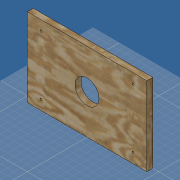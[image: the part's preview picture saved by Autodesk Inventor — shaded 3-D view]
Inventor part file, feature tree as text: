
AUTODESK INVENTOR PART (.ipt)
format: ipt  version: 2019 (Build 230136000, 136)  size: 135,168 bytes
history: native  units: mm
features: extrude x2, other x1, sketch x1
ambient origin geometry x8: Origin, YZ Plane, XZ Plane, XY Plane, X Axis, Y Axis, Z Axis, Center Point
bodies: Volumenkörper1 (feature_tree)
feature tree (4):
  other  "<userpath>\OneDrive\Dokumente\Inventor\Absauganlage\Absauganlage_Params.xlsx"
  sketch  "Skizze1"  dims[d0=364.0mm d1=240.0mm d2=18.0mm d3=0.0mm d5=73.0mm d6=280.0mm d7=180.0mm d8=6.5mm d9=10.0mm d10=0.0mm]
  extrude  "Extrusion1"  Depth=240.0mm
  extrude  "Extrusion2"  Depth=18.0mm
